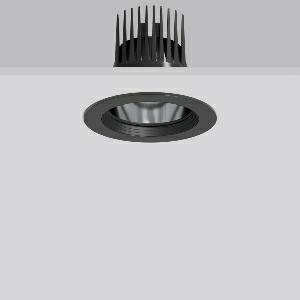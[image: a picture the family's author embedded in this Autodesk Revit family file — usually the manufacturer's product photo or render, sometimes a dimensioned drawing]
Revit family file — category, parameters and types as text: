
# Revit family: heledon_maxi_e_901764_003_1_76_0e8b
name_source: partatom
category: Lighting Fixtures
units: mm (PartAtom-declared; Revit-internal decimal feet)

## family parameters
Cut with Voids When Loaded = No
Host = Face
Light Source = No
Part Type = Normal
Room Calculation Point = No
Round Connector Dimension = Use Diameter
Shared = No

## types (1)
- HELEDON maxi E (1 x LED Modul 940, 4550 lm, 4000)
    Apparent Load = 35 VA
    Approval mark = CE
    CIE Flux Codes = 100 100 100 100 100
    Color Rendering = 92
    Color Temperature = 4000
    Default Elevation = 1800 mm
    Description = Series: HELEDON maxi
Round recessed downlight. Housing: die-cast aluminium, powder-coated. Black plastic ring and recessed LED to prevent glare from the side. Optical assembly with reflector made of MIRO-Silver with 98% total light reflection for outstanding efficiency - can be changed without tools. Best colour rendering index Ra>90. Suitable for Recessed ceiling mounting. Installation without tools thanks to spring fastening system. Including separate LED converter with connecting cable 600 mm.High quality converter without flickering and stroboscopic effect. Through-wiring box (5 pole) available as accessory. The following accessories can be mounted without use of tools: interchangeable lenses, decorative glasses, honeycomb louvre, clear and frosted diffusers, white interchangeable plastic ring. 
Colour: deep black, matt (RAL 9005)
Diameter: 162 mm
Height: 3 mm
Cut-out diameter: 152 mm
Recess height: 200 mm
Luminaire: recess height: 135 mm
Lamp: LED
Socket: without socket
Colour temperature: 4000K
Colour rendering index (CRI): 92
System power: 35 W
Rated luminous flux: 4550 lm
Luminous efficiency: 130 lm/W
Control gear: Converter, dimmable, DALI
Protection class: II
Type of protection: IP 20
    Height = 0 mm  [stored 0 ft]
    Lamp = 1 x LED Modul 940
    Lamp Light Flux = 4550 lm
    Lamp count = 1
    Length = 162 mm
    Lifetime = 50000 h
    Luminous efficacy = 130 lm/W
    Manufacturer = RZB
    ModVariant = No
    Model = 901764.003.1.76
    Mounting Place = Ceiling
    Mounting Type = Recessed
    Number of Poles = 1
    OnlyDefault = Yes
    Power Factor = 1
    Product Name = HELEDON maxi E
    Product group = Recessed downlights
    ProductGroupID = 402
    Protection Class = Protection class II
    Protection Degree = IP 20
    RLX_Detail_Level = 1
    RLX_Emergency_Light_Flux = 0 lm
    RLX_Emergency_Type = 0
    RLX_Emergency_Type_DB = No
    RlxData = <blob elided: 120921 chars, md5=9a6c0799>
    Socket = socket
    Standby Power = 0 W
    System Light Flux = 4550 lm
    System Power = 35 W
    Type Comments = Product without accessories
    Type Image = 901662.003.jpg
    URL = http://relux.com
    VarID = ---
    Voltage = 230 V
    Voltage Range = 220-240 V
    Weight = 0.00 kg
    Width = 0 mm  [stored 0 ft]

note: [stored X ft] marks values corroborated as IEEE doubles in the binary element streams (Revit-internal decimal feet)

## geometry (parser evidence)
native form markers: Blend x4, Sweep x10
no freeform markers — native parametric forms only
